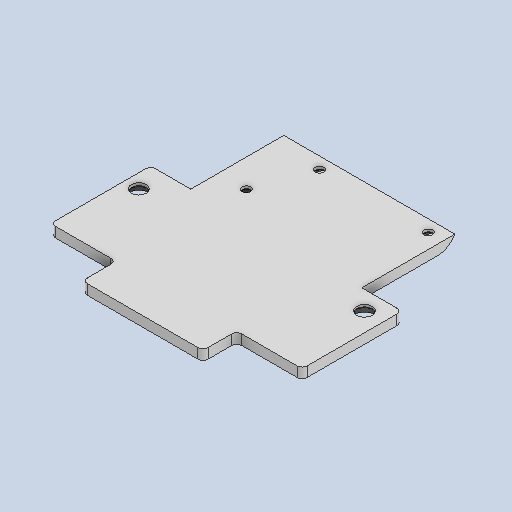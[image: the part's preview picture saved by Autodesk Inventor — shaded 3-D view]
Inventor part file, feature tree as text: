
AUTODESK INVENTOR PART (.ipt)
format: ipt  version: 2023.5 (Build 275446000, 446)  size: 278,528 bytes
history: native  units: mm
features: reference x14, sketch x10, extrude x8, other x6, fillet x4, hole x3, chamfer x2, projected_geometry x2
ambient origin geometry x8: Origin, YZ Plane, XZ Plane, XY Plane, X Axis, Y Axis, Z Axis, Center Point
bodies: Body1 (feature_tree)
feature tree (49):
  other  "Bryła1"
  extrude  "Wyciągnięcie proste1"  Depth=50.0mm
  extrude  "Wyciągnięcie proste3"  Depth=50.0mm
  extrude  "Wyciągnięcie proste5"  Depth=8.0mm
  extrude  "Wyciągnięcie proste6"  Depth=20.0mm
  fillet  "Zaokrąglenie1"  Radius=8.0mm
  extrude  "Wyciągnięcie proste8"  Depth=20.0mm
  extrude  "Wyciągnięcie proste9"  Depth=2.0mm TaperAngle=0.0deg
  sketch  "Szkic11"
  hole  "Otwór1"  [1 undecoded]
  hole  "Otwór2"  [1 undecoded]
  extrude  "Wyciągnięcie proste10"  Depth=8.0mm
  fillet  "Zaokrąglenie2"  Radius=8.0mm
  extrude  "Wyciągnięcie proste11"  TaperAngle=0.0deg  [1 undecoded]
  fillet  "Zaokrąglenie3"  Radius=1.0mm
  fillet  "Zaokrąglenie4"  Radius=10.0mm
  chamfer  "Faza1"  Distance=3.1mm
  hole  "Otwór3"  [1 undecoded]
  chamfer  "Faza2"  [1 undecoded]
  sketch  "Szkic1"
  sketch  "Szkic4"
  reference  "Odniesienie4"
  reference  "Odniesienie5"
  reference  "Odniesienie6"
  reference  "Odniesienie7"
  sketch  "Szkic6"
  projected_geometry  "Pętla rzutowana2"
  reference  "Odniesienie9"
  sketch  "Szkic7"
  projected_geometry  "Pętla rzutowana3"
  reference  "Odniesienie10"
  reference  "Odniesienie11"
  sketch  "Szkic9"
  sketch  "Szkic10"
  reference  "Odniesienie14"
  reference  "Odniesienie15"
  reference  "Odniesienie16"
  reference  "Odniesienie17"
  reference  "Odniesienie18"
  reference  "Odniesienie19"
  sketch  "Szkic12"
  sketch  "Szkic13"
  sketch  "Szkic14"
  reference  "Odniesienie20"
  parser-record x1  (decoder bookkeeping rows leaked as tree rows — omitted from the tree; the rows remain in map.json)
  other  "stratos_v2_mechanics.iam"
  other  "montaz_osi:1"
  other  "nozzyk:1"
  other  "scianka_prawa:1"
note: 5 required parameter values undecoded (feature->parameter linkage not recoverable at this tier; creation-order binding heuristic only, values carry confidence <= 0.55)
note: 1 file-system path scrubbed to <path> (originals preserved in map.json)
